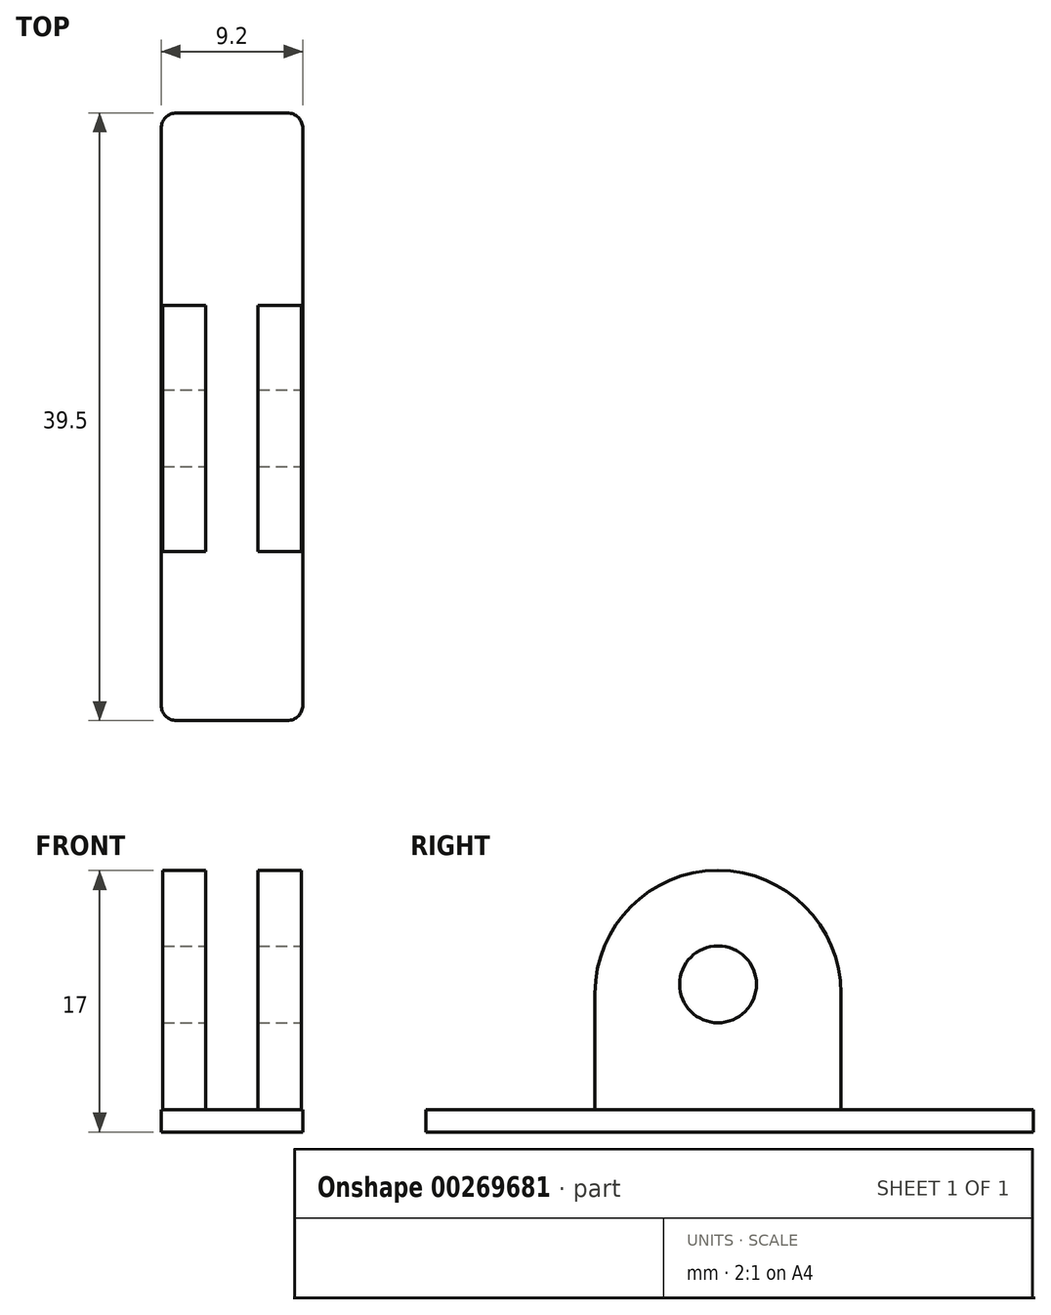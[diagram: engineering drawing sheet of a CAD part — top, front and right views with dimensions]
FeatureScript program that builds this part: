
annotation { "Feature Type Name" : "Feature", "Feature Type Description" : "" }
export const myFeature = defineFeature(function(context is Context, id is Id, definition is map)
    precondition{}
    {
        {
            var Q0;
            Q0=qCreatedBy(makeId("Top.planeOp"),FACE);
            var sketch = newSketch(context, id + "F0", { "sketchPlane" : qUnion([Q0])});
            skLineSegment(sketch, "E0.bottom", {"start": v(1.82, 12) * mm, "end": v(4.62, 12) * mm});
            skLineSegment(sketch, "E0.top", {"start": v(1.82, -4) * mm, "end": v(4.62, -4) * mm});
            skLineSegment(sketch, "E0.left", {"start": v(1.82, 12) * mm, "end": v(1.82, -4) * mm});
            skLineSegment(sketch, "E0.right", {"start": v(4.62, 12) * mm, "end": v(4.62, -4) * mm});
            skLineSegment(sketch, "E1.MirrorCS", {"start": v(-1.58, 12) * mm, "end": v(-1.58, -4) * mm});
            skLineSegment(sketch, "E2.MirrorCS", {"start": v(-1.58, 12) * mm, "end": v(-4.38, 12) * mm});
            skLineSegment(sketch, "E3.MirrorCS", {"start": v(-1.58, -4) * mm, "end": v(-4.38, -4) * mm});
            skLineSegment(sketch, "E4.bottom", {"start": v(-4.48, 24.5) * mm, "end": v(4.72, 24.5) * mm});
            skLineSegment(sketch, "E4.top", {"start": v(-4.48, -15) * mm, "end": v(4.72, -15) * mm});
            skLineSegment(sketch, "E4.left", {"start": v(-4.48, 24.5) * mm, "end": v(-4.48, -15) * mm});
            skLineSegment(sketch, "E4.right", {"start": v(4.72, 24.5) * mm, "end": v(4.72, -15) * mm});
            skLineSegment(sketch, "E5.bottom", {"start": v(-4.38, 12) * mm, "end": v(-4.38, 12) * mm});
            skLineSegment(sketch, "E5.top", {"start": v(-4.38, -4) * mm, "end": v(-4.38, -4) * mm});
            skLineSegment(sketch, "E5.left", {"start": v(-4.38, 12) * mm, "end": v(-4.38, -4) * mm});
            skLineSegment(sketch, "E5.right", {"start": v(-4.38, 12) * mm, "end": v(-4.38, -4) * mm});
            skSolve(sketch);
        }
        {
            var Q0;
            Q0=makeQuery(id+"F0.imprint","IMPRINT",FACE,{"disambiguationData":[TD([[makeQuery(id+"F0.imprint","IMPRINT",EDGE,{"derivedFrom":sQuery(id+"F0.wireOp",EDGE,"E0.bottom")}),1.0]])]});
            extrude(context, id + "F1", {"entities" : qUnion([Q0]), "depth" : 1.45 * mm});
        }
        {
            var Q0;
            Q0=makeQuery(id+"F0.imprint","IMPRINT",FACE,{"disambiguationData":[TD([[makeQuery(id+"F0.imprint","IMPRINT",EDGE,{"derivedFrom":sQuery(id+"F0.wireOp",EDGE,"E1.MirrorCS")}),-1.0]])]});
            var Q1;
            Q1=makeQuery(id+"F0.imprint","IMPRINT",FACE,{"disambiguationData":[TD([[makeQuery(id+"F0.imprint","IMPRINT",EDGE,{"derivedFrom":sQuery(id+"F0.wireOp",EDGE,"E0.bottom")}),-1.0]])]});
            extrude(context, id + "F2", {"entities" : qUnion([Q0, Q1]), "operationType" : NewBodyOperationType.ADD, "depth" : 17 * mm});
        }
        {
            var Q0;
            Q0=makeQuery(id+"F2.opExtrude","CAP_EDGE",EDGE,{"disambiguationData":[OSD([sQuery(id+"F0.wireOp",EDGE,"E2.MirrorCS")])],"isStart":false});
            var Q1;
            Q1=makeQuery(id+"F2.opExtrude","CAP_EDGE",EDGE,{"disambiguationData":[OSD([sQuery(id+"F0.wireOp",EDGE,"E0.bottom")])],"isStart":false});
            var Q2;
            Q2=makeQuery(id+"F2.opExtrude","CAP_EDGE",EDGE,{"disambiguationData":[OSD([sQuery(id+"F0.wireOp",EDGE,"E0.top")])],"isStart":false});
            var Q3;
            Q3=makeQuery(id+"F2.opExtrude","CAP_EDGE",EDGE,{"disambiguationData":[OSD([sQuery(id+"F0.wireOp",EDGE,"E3.MirrorCS")])],"isStart":false});
            fillet(context, id + "F3", {"entities" : qUnion([Q0, Q1, Q2, Q3]), "radius" : 8 * mm, "tangentPropagation" : true, "allowEdgeOverflow" : false});
        }
        {
            var Q0;
            Q0=makeQuery(id+"F2.opExtrude","SWEPT_FACE",FACE,{"disambiguationData":[OSD([sQuery(id+"F0.wireOp",EDGE,"E0.right")])]});
            var sketch = newSketch(context, id + "F4", { "sketchPlane" : qUnion([Q0])});
            skCircle(sketch, "E6", {"center": v(4, 9.6) * mm, "radius": 2.5 * mm});
            skPoint(sketch, "E6.centerSnap0", {"position": v(4, 17) * mm});
            skSolve(sketch);
        }
        {
            var Q0;
            Q0=makeQuery(id+"F4.imprint","IMPRINT",FACE,{"disambiguationData":[TD([[makeQuery(id+"F4.imprint","IMPRINT",EDGE,{"derivedFrom":sQuery(id+"F4.wireOp",EDGE,"E6")}),1.0]])]});
            extrude(context, id + "F5", {"entities" : qUnion([Q0]), "operationType" : NewBodyOperationType.REMOVE, "oppositeDirection" : true, "depth" : 25 * mm});
        }
        {
            var Q0;
            Q0=makeQuery(id+"F1.opExtrude","SWEPT_EDGE",EDGE,{"disambiguationData":[OSD([sQuery(id+"F0.wireOp",EDGE,"E4.bottom"),sQuery(id+"F0.wireOp",EDGE,"E4.right")])]});
            var Q1;
            Q1=makeQuery(id+"F1.opExtrude","SWEPT_EDGE",EDGE,{"disambiguationData":[OSD([sQuery(id+"F0.wireOp",EDGE,"E4.bottom"),sQuery(id+"F0.wireOp",EDGE,"E4.left")])]});
            var Q2;
            Q2=makeQuery(id+"F1.opExtrude","SWEPT_EDGE",EDGE,{"disambiguationData":[OSD([sQuery(id+"F0.wireOp",EDGE,"E4.top"),sQuery(id+"F0.wireOp",EDGE,"E4.right")])]});
            var Q3;
            Q3=makeQuery(id+"F1.opExtrude","SWEPT_EDGE",EDGE,{"disambiguationData":[OSD([sQuery(id+"F0.wireOp",EDGE,"E4.top"),sQuery(id+"F0.wireOp",EDGE,"E4.left")])]});
            fillet(context, id + "F6", {"entities" : qUnion([Q0, Q1, Q2, Q3]), "radius" : 1 * mm, "tangentPropagation" : true, "allowEdgeOverflow" : false});
        }
    });
